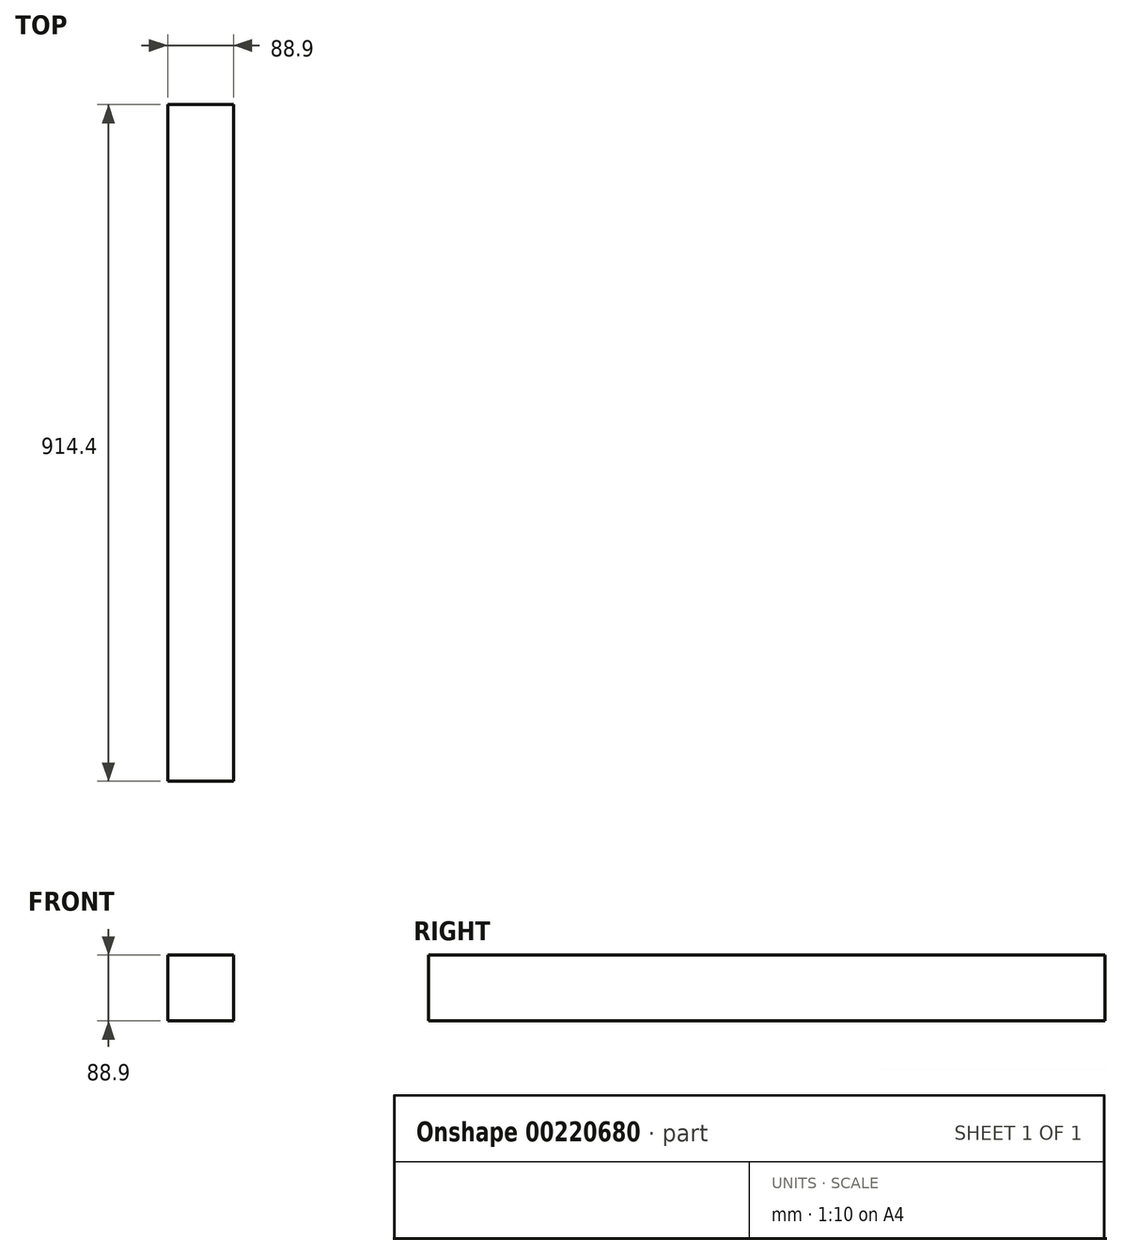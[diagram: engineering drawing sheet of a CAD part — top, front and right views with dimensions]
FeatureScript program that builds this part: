
annotation { "Feature Type Name" : "Feature", "Feature Type Description" : "" }
export const myFeature = defineFeature(function(context is Context, id is Id, definition is map)
    precondition{}
    {
        {
            var Q0;
            Q0=qCreatedBy(makeId("Top.planeOp"),FACE);
            var sketch = newSketch(context, id + "F0", { "sketchPlane" : qUnion([Q0])});
            skLineSegment(sketch, "E0.bottom", {"start": v(44.45, -457.2) * mm, "end": v(-44.45, -457.2) * mm});
            skLineSegment(sketch, "E0.top", {"start": v(44.45, 457.2) * mm, "end": v(-44.45, 457.2) * mm});
            skLineSegment(sketch, "E0.left", {"start": v(44.45, -457.2) * mm, "end": v(44.45, 457.2) * mm});
            skLineSegment(sketch, "E0.right", {"start": v(-44.45, -457.2) * mm, "end": v(-44.45, 457.2) * mm});
            skPoint(sketch, "E0.middle", {"position": v(0, 0) * mm});
            skSolve(sketch);
        }
        {
            var Q0;
            Q0 = qSketchRegion(id + "F0", true);
            extrude(context, id + "F1", {"entities" : qUnion([Q0]), "depth" : 88.9 * mm});
        }
    });
